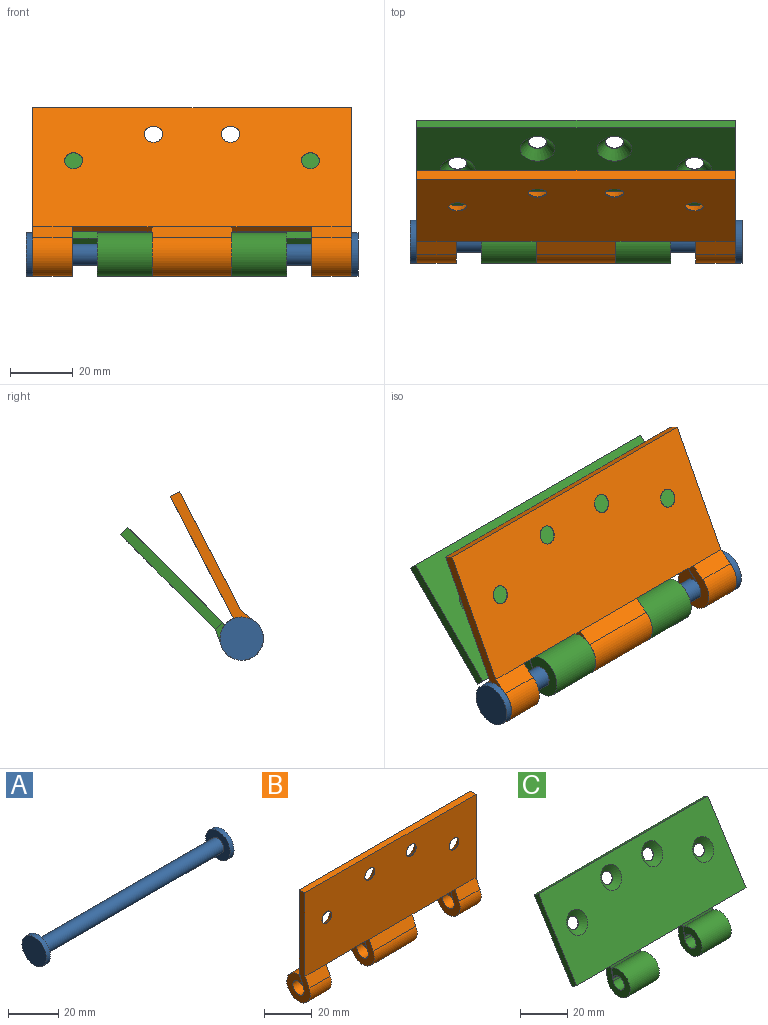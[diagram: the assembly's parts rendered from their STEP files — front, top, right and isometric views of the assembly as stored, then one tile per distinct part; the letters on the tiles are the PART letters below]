
ASSEMBLY  parts=3 mates=2
PART A: 7 faces, bbox 106x13.8x13.8 mm
  f0: cylinder r=3.37mm len=101.6mm, axis (1,0,0), area 2153.5mm2, adj f3,f6
  f1: cylinder r=6.91mm len=13.82mm, axis (1,0,0), area 94.8mm2, adj f2,f3
  f2: plane 13.82x13.82mm, normal (-1,0,0), area 150mm2, adj f1
  f3: plane 13.82x13.82mm, normal (1,0,0), area 114.2mm2, adj f0,f1
  f4: cylinder r=6.91mm len=13.82mm, axis (1,0,0), area 94.8mm2, adj f5,f6
  f5: plane 13.82x13.82mm, normal (1,0,0), area 150mm2, adj f4
  f6: plane 13.82x13.82mm, normal (-1,0,0), area 114.2mm2, adj f0,f4
PART B: 34 faces, bbox 101.6x13.9x57.7 mm
  f0: plane 12.55x4.6mm, normal (0,-0.93,0.36), area 61.7mm2, adj f1,f10,f19,f23
  f1: cylinder r=3.37mm len=12.55mm, axis (-1,0,0), area 249.4mm2, adj f0,f2,f19,f23
  f2: plane 12.55x6.74mm, normal (0,0.93,-0.36), area 90.5mm2, adj f1,f14,f19,f23
  f3: plane 12.55x4.9mm, normal (0,-0.9,0.44), area 68.3mm2, adj f10,f16,f19,f23
  f4: cylinder r=6.95mm len=25.5mm, axis (-1,0,0), area 932.9mm2, adj f6,f9,f21,f24
  f5: cylinder r=6.95mm len=13.89mm, axis (-1,0,0), area 459mm2, adj f11,f17,f18,f22
  f6: plane 25.5x4.6mm, normal (0,-0.93,0.36), area 125.5mm2, adj f4,f7,f21,f24
  f7: cylinder r=3.37mm len=25.5mm, axis (-1,0,0), area 506.9mm2, adj f6,f8,f21,f24
  f8: plane 25.5x6.74mm, normal (0,0.93,-0.36), area 183.8mm2, adj f7,f14,f21,f24
  f9: plane 25.5x4.9mm, normal (0,-0.9,0.44), area 138.9mm2, adj f4,f16,f21,f24
  f10: cylinder r=6.95mm len=13.89mm, axis (-1,0,0), area 459mm2, adj f0,f3,f19,f23
  f11: plane 12.55x4.6mm, normal (0,-0.93,0.36), area 61.7mm2, adj f5,f12,f18,f22
  f12: cylinder r=3.37mm len=12.55mm, axis (-1,0,0), area 249.4mm2, adj f11,f13,f18,f22
  f13: plane 12.55x6.74mm, normal (0,0.93,-0.36), area 90.5mm2, adj f12,f14,f18,f22
  f14: plane 101.6x42.86mm, normal (0,1,0), area 3966mm2, adj f2,f8,f13,f15,f18,f19,f20,f25
  f15: plane 101.6x3.28mm, normal (0,0,1), area 332.9mm2, adj f14,f16,f18,f19
  f16: plane 101.6x42.86mm, normal (0,-1,0), area 4249.5mm2, adj f3,f9,f15,f17,f18,f19,f20,f25
  f17: plane 12.55x4.9mm, normal (0,-0.9,0.44), area 68.3mm2, adj f5,f16,f18,f22
  f18: plane 57.75x13.89mm, normal (1,0,0), area 261.4mm2, adj f5,f11,f12,f13,f14,f15,f16,f17
  f19: plane 57.75x13.89mm, normal (-1,0,0), area 261.4mm2, adj f0,f1,f2,f3,f10,f14,f15,f16
  f20: plane 25.5x3.28mm, normal (0,0,-1), area 83.6mm2, adj f14,f16,f21,f22
  f21: plane 14.88x13.89mm, normal (1,0,0), area 120.9mm2, adj f4,f6,f7,f8,f9,f20
  f22: plane 14.88x13.89mm, normal (-1,0,0), area 120.9mm2, adj f5,f11,f12,f13,f17,f20
  f23: plane 14.88x13.89mm, normal (1,0,0), area 120.9mm2, adj f0,f1,f2,f3,f10,f25
  f24: plane 14.88x13.89mm, normal (-1,0,0), area 120.9mm2, adj f4,f6,f7,f8,f9,f25
  f25: plane 25.5x3.28mm, normal (0,0,-1), area 83.6mm2, adj f14,f16,f23,f24
  f26: cylinder r=2.9mm len=5.79mm, axis (0,1,0), area 3.8mm2, adj f16,f27
  f27: cone r=5.56mm half-angle=41deg, axis (0,1,0), area 108mm2, adj f14,f26
  f28: cylinder r=2.9mm len=5.79mm, axis (0,1,0), area 3.8mm2, adj f16,f29
  f29: cone r=5.56mm half-angle=41deg, axis (0,1,0), area 108mm2, adj f14,f28
  f30: cylinder r=2.9mm len=5.79mm, axis (0,1,0), area 3.8mm2, adj f16,f31
  f31: cone r=5.56mm half-angle=41deg, axis (0,1,0), area 108mm2, adj f14,f30
  f32: cylinder r=2.9mm len=5.79mm, axis (0,1,0), area 3.8mm2, adj f16,f33
  f33: cone r=5.56mm half-angle=41deg, axis (0,1,0), area 108mm2, adj f14,f32
PART C: 30 faces, bbox 101.6x37.2x49.6 mm
  f0: plane 14.44x13.89mm, normal (1,0,0), area 120.9mm2, adj f3,f4,f5,f6,f7,f11
  f1: plane 101.6x2.77mm, normal (0,0.53,0.85), area 332.9mm2, adj f2,f8,f9,f18
  f2: plane 101.6x36.29mm, normal (0,-0.85,0.53), area 3966mm2, adj f1,f3,f9,f10,f11,f13,f18,f19
  f3: plane 17.56x7.07mm, normal (0,-0.98,0.2), area 126.6mm2, adj f0,f2,f4,f21
  f4: cylinder r=3.37mm len=17.56mm, axis (-1,0,0), area 349.1mm2, adj f0,f3,f5,f21
  f5: plane 17.56x4.83mm, normal (0,0.98,-0.2), area 86.4mm2, adj f0,f4,f6,f21
  f6: cylinder r=6.95mm len=17.56mm, axis (-1,0,0), area 642.5mm2, adj f0,f5,f7,f21
  f7: plane 17.56x5.42mm, normal (0,0.99,-0.11), area 95.7mm2, adj f0,f6,f8,f21
  f8: plane 101.6x36.29mm, normal (0,0.85,-0.53), area 4249.5mm2, adj f1,f7,f9,f10,f11,f17,f18,f19
  f9: plane 38.03x25.58mm, normal (-1,0,0), area 140.4mm2, adj f1,f2,f8,f10
  f10: plane 20.49x2.77mm, normal (0,-0.53,-0.85), area 67.1mm2, adj f2,f8,f9,f21
  f11: plane 25.5x2.77mm, normal (0,-0.53,-0.85), area 83.6mm2, adj f0,f2,f8,f12
  f12: plane 14.44x13.89mm, normal (-1,0,0), area 120.9mm2, adj f11,f13,f14,f15,f16,f17
  f13: plane 17.56x7.07mm, normal (0,-0.98,0.2), area 126.6mm2, adj f2,f12,f14,f20
  f14: cylinder r=3.37mm len=17.56mm, axis (1,0,0), area 349.1mm2, adj f12,f13,f15,f20
  f15: plane 17.56x4.83mm, normal (0,0.98,-0.2), area 86.4mm2, adj f12,f14,f16,f20
  f16: cylinder r=6.95mm len=17.56mm, axis (1,0,0), area 642.5mm2, adj f12,f15,f17,f20
  f17: plane 17.56x5.42mm, normal (0,0.99,-0.11), area 95.7mm2, adj f8,f12,f16,f20
  f18: plane 38.03x25.58mm, normal (1,0,0), area 140.4mm2, adj f1,f2,f8,f19
  f19: plane 20.49x2.77mm, normal (0,-0.53,-0.85), area 67.1mm2, adj f2,f8,f18,f20
  f20: plane 14.44x13.89mm, normal (1,0,0), area 120.9mm2, adj f13,f14,f15,f16,f17,f19
  f21: plane 14.44x13.89mm, normal (-1,0,0), area 120.9mm2, adj f3,f4,f5,f6,f7,f10
  f22: cone r=5.56mm half-angle=41deg, axis (0,-0.85,0.53), area 108mm2, adj f2,f23
  f23: cylinder r=2.9mm len=5.79mm, axis (0,-0.85,0.53), area 3.8mm2, adj f8,f22
  f24: cone r=5.56mm half-angle=41deg, axis (0,-0.85,0.53), area 108mm2, adj f2,f25
  f25: cylinder r=2.9mm len=5.79mm, axis (0,-0.85,0.53), area 3.8mm2, adj f8,f24
  f26: cone r=5.56mm half-angle=41deg, axis (0,-0.85,0.53), area 108mm2, adj f2,f27
  f27: cylinder r=2.9mm len=5.79mm, axis (0,-0.85,0.53), area 3.8mm2, adj f8,f26
  f28: cone r=5.56mm half-angle=41deg, axis (0,-0.85,0.53), area 108mm2, adj f2,f29
  f29: cylinder r=2.9mm len=5.79mm, axis (0,-0.85,0.53), area 3.8mm2, adj f8,f28
PLACE A t=(-54.28,-77.75,47.32)mm
PLACE B rot(axis=(-1,0,0),27.3deg) t=(-54.28,-115.15,85.01)mm
PLACE C rot(axis=(-1,0,0),12.9deg) t=(-54.28,-97.61,62.84)mm
MATE revolute B.f1 <-> A.f0  axis (-1,0,0) through (-97.82,-18.8,143.22)mm
MATE revolute C.f14 <-> B.f1  axis (1,0,0) through (-59.77,-18.8,143.22)mm
